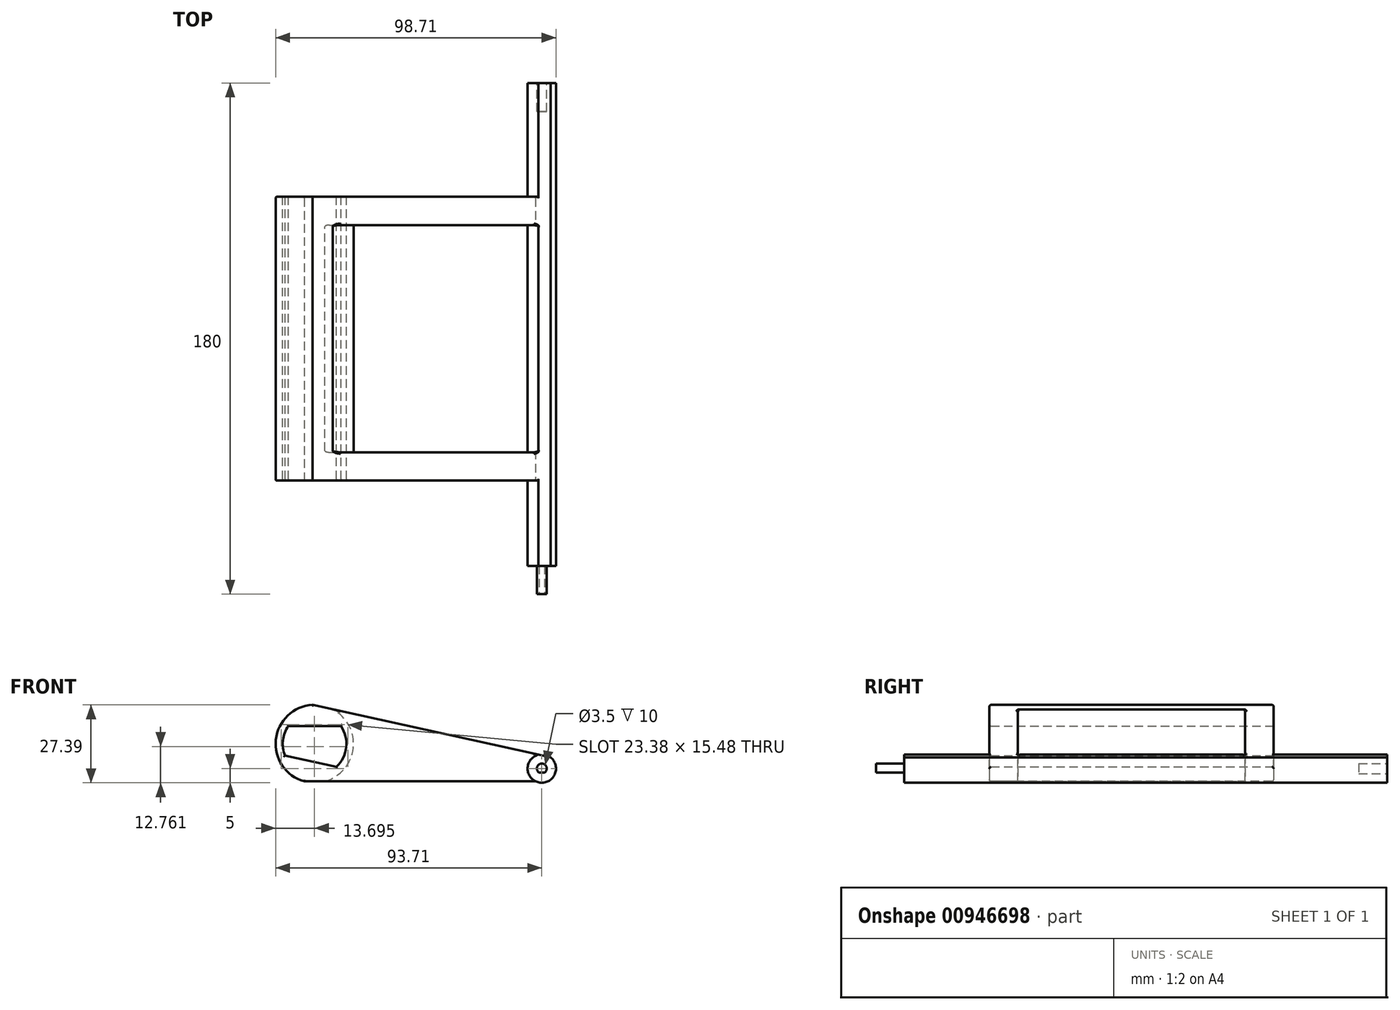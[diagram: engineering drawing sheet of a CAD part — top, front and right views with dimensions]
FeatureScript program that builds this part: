
annotation { "Feature Type Name" : "Feature", "Feature Type Description" : "" }
export const myFeature = defineFeature(function(context is Context, id is Id, definition is map)
    precondition{}
    {
        {
            var Q0;
            Q0=qCreatedBy(makeId("Front.planeOp"),FACE);
            var sketch = newSketch(context, id + "F0", { "sketchPlane" : qUnion([Q0])});
            skCircle(sketch, "E0", {"center": v(0, 0) * mm, "radius": 5 * mm});
            skCircle(sketch, "E1", {"center": v(-80, 8.7) * mm, "radius": 13.7 * mm});
            skLineSegment(sketch, "E2", {"start": v(-80, -5) * mm, "end": v(0, -5) * mm});
            skLineSegment(sketch, "E3", {"start": v(-77.05, 22.1) * mm, "end": v(1.08, 4.88) * mm});
            skCircle(sketch, "E4.0", {"center": v(-80, 8.7) * mm, "radius": 11.2 * mm});
            skLineSegment(sketch, "E5", {"start": v(-89.27, 15) * mm, "end": v(-70.73, 15) * mm});
            skLineSegment(sketch, "E6", {"start": v(-90.41, 4.56) * mm, "end": v(-72.3, 0.57) * mm});
            skSolve(sketch);
        }
        {
            var Q0;
            Q0=makeQuery(id+"F0.imprint","IMPRINT",FACE,{"disambiguationData":[TD([[makeQuery(id+"F0.imprint","IMPRINT",EDGE,{"derivedFrom":sQuery(id+"F0.wireOp",EDGE,"E0")}),1.0]])]});
            extrude(context, id + "F1", {"entities" : qUnion([Q0]), "depth" : 180 * mm, "offsetDistance" : 25 * mm, "symmetric" : true});
        }
        {
            var Q0;
            {var subQ0=sQuery(id+"F0.wireOp",EDGE,"E1");var subQ1=makeQuery(id+"F0.imprint","INTERSECT",VERTEX,{"derivedFrom":[subQ0,sQuery(id+"F0.wireOp",EDGE,"E2")]});Q0=makeQuery(id+"F0.imprint","IMPRINT",FACE,{"disambiguationData":[TD([[makeQuery(id+"F0.imprint","IMPRINT",EDGE,{"disambiguationData":[TD([[subQ1,1.0]])],"derivedFrom":subQ0}),1.0]])]});}
            var Q1;
            {var subQ0=sQuery(id+"F0.wireOp",EDGE,"E2");Q1=makeQuery(id+"F0.imprint","IMPRINT",FACE,{"disambiguationData":[TD([[makeQuery(id+"F0.imprint","IMPRINT",EDGE,{"derivedFrom":subQ0}),1.0]])]});}
            var Q2;
            {var subQ0=sQuery(id+"F0.wireOp",EDGE,"E5");Q2=makeQuery(id+"F0.imprint","IMPRINT",FACE,{"disambiguationData":[TD([[makeQuery(id+"F0.imprint","IMPRINT",EDGE,{"derivedFrom":subQ0}),1.0]])]});}
            var Q3;
            {var subQ0=sQuery(id+"F0.wireOp",EDGE,"E6");Q3=makeQuery(id+"F0.imprint","IMPRINT",FACE,{"disambiguationData":[TD([[makeQuery(id+"F0.imprint","IMPRINT",EDGE,{"derivedFrom":subQ0}),-1.0]])]});}
            extrude(context, id + "F2", {"entities" : qUnion([Q0, Q1, Q2, Q3]), "operationType" : NewBodyOperationType.ADD, "depth" : 100 * mm, "offsetDistance" : 25 * mm, "symmetric" : true});
        }
        {
            var Q0;
            {var subQ0=sQuery(id+"F0.wireOp",EDGE,"E2");Q0=makeQuery(id+"F0.imprint","IMPRINT",FACE,{"disambiguationData":[TD([[makeQuery(id+"F0.imprint","IMPRINT",EDGE,{"derivedFrom":subQ0}),1.0]])]});}
            extrude(context, id + "F3", {"entities" : qUnion([Q0]), "operationType" : NewBodyOperationType.REMOVE, "oppositeDirection" : true, "depth" : 80 * mm, "offsetDistance" : 25 * mm, "symmetric" : true});
        }
        {
            var Q0;
            Q0=makeQuery(id+"F1.opExtrude","CAP_FACE",FACE,{"disambiguationData":[OSD([sQuery(id+"F0.wireOp",EDGE,"E0")])],"isStart":false});
            var sketch = newSketch(context, id + "F4", { "sketchPlane" : qUnion([Q0])});
            skArc(sketch, "E7.0.0", {"start": v(-77.05, 22.1) * mm, "mid": v(-93.63, 10.2) * mm, "end": v(-80, -5) * mm});
            skLineSegment(sketch, "E7.0.1", {"start": v(-80, -5) * mm, "end": v(0, -5) * mm});
            skArc(sketch, "E7.0.2", {"start": v(0, -5) * mm, "mid": v(-4.97, 0.54) * mm, "end": v(1.08, 4.88) * mm});
            skLineSegment(sketch, "E7.0.3", {"start": v(1.08, 4.88) * mm, "end": v(-77.05, 22.1) * mm});
            skCircle(sketch, "E8.0", {"center": v(0, 0) * mm, "radius": 5 * mm});
            skLineSegment(sketch, "E9", {"start": v(-89.59, -4.5) * mm, "end": v(11.55, -4.5) * mm});
            skLineSegment(sketch, "E10", {"start": v(-84.5, 23.22) * mm, "end": v(10.9, 2.2) * mm});
            skSolve(sketch);
        }
        {
            var Q0;
            {var subQ0=sQuery(id+"F4.wireOp",EDGE,"E7.0.1");Q0=makeQuery(id+"F4.imprint","IMPRINT",FACE,{"disambiguationData":[TD([[makeQuery(id+"F4.imprint","IMPRINT",EDGE,{"derivedFrom":subQ0}),1.0]])]});}
            var Q1;
            {var subQ0=sQuery(id+"F4.wireOp",EDGE,"E8.0");var subQ1=makeQuery(id+"F4.imprint","INTERSECT",VERTEX,{"derivedFrom":[sQuery(id+"F4.wireOp",EDGE,"E7.0.1"),subQ0]});Q1=makeQuery(id+"F4.imprint","IMPRINT",FACE,{"disambiguationData":[TD([[makeQuery(id+"F4.imprint","IMPRINT",EDGE,{"disambiguationData":[TD([[subQ1,1.0]])],"derivedFrom":subQ0}),1.0]])]});}
            extrude(context, id + "F5", {"entities" : qUnion([Q0, Q1]), "operationType" : NewBodyOperationType.REMOVE, "endBound" : BoundingType.THROUGH_ALL, "oppositeDirection" : true, "depth" : 25 * mm, "offsetDistance" : 25 * mm});
        }
        {
            var Q0;
            {var subQ0=sQuery(id+"F4.wireOp",EDGE,"E7.0.3");Q0=makeQuery(id+"F4.imprint","IMPRINT",FACE,{"disambiguationData":[TD([[makeQuery(id+"F4.imprint","IMPRINT",EDGE,{"derivedFrom":subQ0}),1.0]])]});}
            var Q1;
            {var subQ0=sQuery(id+"F4.wireOp",EDGE,"E8.0");var subQ1=makeQuery(id+"F4.imprint","INTERSECT",VERTEX,{"derivedFrom":[sQuery(id+"F4.wireOp",EDGE,"E7.0.3"),subQ0]});Q1=makeQuery(id+"F4.imprint","IMPRINT",FACE,{"disambiguationData":[TD([[makeQuery(id+"F4.imprint","IMPRINT",EDGE,{"disambiguationData":[TD([[subQ1,1.0]])],"derivedFrom":subQ0}),1.0]])]});}
            extrude(context, id + "F6", {"entities" : qUnion([Q0, Q1]), "operationType" : NewBodyOperationType.REMOVE, "endBound" : BoundingType.THROUGH_ALL, "oppositeDirection" : true, "depth" : 25 * mm, "offsetDistance" : 25 * mm});
        }
        {
            var Q0;
            Q0=makeQuery(id+"F2.opExtrude","CAP_EDGE",EDGE,{"disambiguationData":[OSD([sQuery(id+"F0.wireOp",EDGE,"E1")])],"isStart":false});
            var Q1;
            Q1=makeQuery(id+"F2.opExtrude","CAP_EDGE",EDGE,{"disambiguationData":[OSD([sQuery(id+"F0.wireOp",EDGE,"E1")])],"isStart":true});
            var Q2;
            {var subQ0=sQuery(id+"F0.wireOp",EDGE,"E4.0");Q2=makeQuery(id+"F2.opExtrude","CAP_EDGE",EDGE,{"disambiguationData":[OSD([subQ0]),TDD([makeQuery(id+"F0.imprint","IMPRINT",EDGE,{"disambiguationData":[TD([[makeQuery(id+"F0.imprint","INTERSECT",VERTEX,{"disambiguationData":[OD(0.0)],"derivedFrom":[subQ0,sQuery(id+"F0.wireOp",EDGE,"E5")]}),-1.0]])],"derivedFrom":subQ0})])],"isStart":false});}
            var Q3;
            {var subQ0=sQuery(id+"F0.wireOp",EDGE,"E4.0");Q3=makeQuery(id+"F2.opExtrude","CAP_EDGE",EDGE,{"disambiguationData":[OSD([subQ0]),TDD([makeQuery(id+"F0.imprint","IMPRINT",EDGE,{"disambiguationData":[TD([[makeQuery(id+"F0.imprint","INTERSECT",VERTEX,{"disambiguationData":[OD(1.0)],"derivedFrom":[subQ0,sQuery(id+"F0.wireOp",EDGE,"E5")]}),1.0]])],"derivedFrom":subQ0})])],"isStart":false});}
            var Q4;
            Q4=makeQuery(id+"F2.opExtrude","CAP_EDGE",EDGE,{"disambiguationData":[OSD([sQuery(id+"F0.wireOp",EDGE,"E5")])],"isStart":false});
            var Q5;
            Q5=makeQuery(id+"F2.opExtrude","CAP_EDGE",EDGE,{"disambiguationData":[OSD([sQuery(id+"F0.wireOp",EDGE,"E6")])],"isStart":false});
            var Q6;
            Q6=makeQuery(id+"F2.opExtrude","CAP_EDGE",EDGE,{"disambiguationData":[OSD([sQuery(id+"F0.wireOp",EDGE,"E6")])],"isStart":true});
            var Q7;
            {var subQ0=sQuery(id+"F0.wireOp",EDGE,"E4.0");Q7=makeQuery(id+"F2.opExtrude","CAP_EDGE",EDGE,{"disambiguationData":[OSD([subQ0]),TDD([makeQuery(id+"F0.imprint","IMPRINT",EDGE,{"disambiguationData":[TD([[makeQuery(id+"F0.imprint","INTERSECT",VERTEX,{"disambiguationData":[OD(1.0)],"derivedFrom":[subQ0,sQuery(id+"F0.wireOp",EDGE,"E5")]}),1.0]])],"derivedFrom":subQ0})])],"isStart":true});}
            var Q8;
            {var subQ0=sQuery(id+"F0.wireOp",EDGE,"E4.0");Q8=makeQuery(id+"F2.opExtrude","CAP_EDGE",EDGE,{"disambiguationData":[OSD([subQ0]),TDD([makeQuery(id+"F0.imprint","IMPRINT",EDGE,{"disambiguationData":[TD([[makeQuery(id+"F0.imprint","INTERSECT",VERTEX,{"disambiguationData":[OD(0.0)],"derivedFrom":[subQ0,sQuery(id+"F0.wireOp",EDGE,"E5")]}),-1.0]])],"derivedFrom":subQ0})])],"isStart":true});}
            var Q9;
            Q9=makeQuery(id+"F2.opExtrude","CAP_EDGE",EDGE,{"disambiguationData":[OSD([sQuery(id+"F0.wireOp",EDGE,"E5")])],"isStart":true});
            var Q10;
            Q10=makeQuery(id+"F6.boolean.opBoolean","INTERSECT",EDGE,{"derivedFrom":[makeQuery(id+"F2.opExtrude","CAP_FACE",FACE,{"disambiguationData":[OSD([sQuery(id+"F0.wireOp",EDGE,"E0"),sQuery(id+"F0.wireOp",EDGE,"E1"),sQuery(id+"F0.wireOp",EDGE,"E2"),sQuery(id+"F0.wireOp",EDGE,"E3"),sQuery(id+"F0.wireOp",EDGE,"E4.0"),sQuery(id+"F0.wireOp",EDGE,"E5"),sQuery(id+"F0.wireOp",EDGE,"E6")])],"isStart":false}),makeQuery(id+"F6.opExtrude","SWEPT_FACE",FACE,{"disambiguationData":[OSD([sQuery(id+"F4.wireOp",EDGE,"E10")])]})]});
            var Q11;
            Q11=makeQuery(id+"F5.boolean.opBoolean","INTERSECT",EDGE,{"derivedFrom":[makeQuery(id+"F2.opExtrude","CAP_FACE",FACE,{"disambiguationData":[OSD([sQuery(id+"F0.wireOp",EDGE,"E0"),sQuery(id+"F0.wireOp",EDGE,"E1"),sQuery(id+"F0.wireOp",EDGE,"E2"),sQuery(id+"F0.wireOp",EDGE,"E3"),sQuery(id+"F0.wireOp",EDGE,"E4.0"),sQuery(id+"F0.wireOp",EDGE,"E5"),sQuery(id+"F0.wireOp",EDGE,"E6")])],"isStart":false}),makeQuery(id+"F5.opExtrude","SWEPT_FACE",FACE,{"disambiguationData":[OSD([sQuery(id+"F4.wireOp",EDGE,"E9")])]})]});
            var Q12;
            Q12=makeQuery(id+"F6.boolean.opBoolean","INTERSECT",EDGE,{"derivedFrom":[makeQuery(id+"F3.boolean.opBoolean","COPY",FACE,{"derivedFrom":makeQuery(id+"F3.opExtrude","CAP_FACE",FACE,{"disambiguationData":[OSD([sQuery(id+"F0.wireOp",EDGE,"E0"),sQuery(id+"F0.wireOp",EDGE,"E1"),sQuery(id+"F0.wireOp",EDGE,"E2"),sQuery(id+"F0.wireOp",EDGE,"E3")])],"isStart":true})}),makeQuery(id+"F6.opExtrude","SWEPT_FACE",FACE,{"disambiguationData":[OSD([sQuery(id+"F4.wireOp",EDGE,"E10")])]})]});
            var Q13;
            Q13=makeQuery(id+"F6.boolean.opBoolean","INTERSECT",EDGE,{"derivedFrom":[makeQuery(id+"F2.opExtrude","CAP_FACE",FACE,{"disambiguationData":[OSD([sQuery(id+"F0.wireOp",EDGE,"E0"),sQuery(id+"F0.wireOp",EDGE,"E1"),sQuery(id+"F0.wireOp",EDGE,"E2"),sQuery(id+"F0.wireOp",EDGE,"E3"),sQuery(id+"F0.wireOp",EDGE,"E4.0"),sQuery(id+"F0.wireOp",EDGE,"E5"),sQuery(id+"F0.wireOp",EDGE,"E6")])],"isStart":true}),makeQuery(id+"F6.opExtrude","SWEPT_FACE",FACE,{"disambiguationData":[OSD([sQuery(id+"F4.wireOp",EDGE,"E10")])]})]});
            var Q14;
            Q14=makeQuery(id+"F5.boolean.opBoolean","INTERSECT",EDGE,{"derivedFrom":[makeQuery(id+"F2.opExtrude","CAP_FACE",FACE,{"disambiguationData":[OSD([sQuery(id+"F0.wireOp",EDGE,"E0"),sQuery(id+"F0.wireOp",EDGE,"E1"),sQuery(id+"F0.wireOp",EDGE,"E2"),sQuery(id+"F0.wireOp",EDGE,"E3"),sQuery(id+"F0.wireOp",EDGE,"E4.0"),sQuery(id+"F0.wireOp",EDGE,"E5"),sQuery(id+"F0.wireOp",EDGE,"E6")])],"isStart":true}),makeQuery(id+"F5.opExtrude","SWEPT_FACE",FACE,{"disambiguationData":[OSD([sQuery(id+"F4.wireOp",EDGE,"E9")])]})]});
            var Q15;
            Q15=makeQuery(id+"F6.boolean.opBoolean","INTERSECT",EDGE,{"derivedFrom":[makeQuery(id+"F3.boolean.opBoolean","COPY",FACE,{"derivedFrom":makeQuery(id+"F3.opExtrude","CAP_FACE",FACE,{"disambiguationData":[OSD([sQuery(id+"F0.wireOp",EDGE,"E0"),sQuery(id+"F0.wireOp",EDGE,"E1"),sQuery(id+"F0.wireOp",EDGE,"E2"),sQuery(id+"F0.wireOp",EDGE,"E3")])],"isStart":false})}),makeQuery(id+"F6.opExtrude","SWEPT_FACE",FACE,{"disambiguationData":[OSD([sQuery(id+"F4.wireOp",EDGE,"E10")])]})]});
            var Q16;
            Q16=makeQuery(id+"F3.boolean.opBoolean","COPY",EDGE,{"derivedFrom":makeQuery(id+"F3.opExtrude","CAP_EDGE",EDGE,{"disambiguationData":[OSD([sQuery(id+"F0.wireOp",EDGE,"E1")])],"isStart":false})});
            var Q17;
            Q17=makeQuery(id+"F3.boolean.opBoolean","COPY",EDGE,{"derivedFrom":makeQuery(id+"F3.opExtrude","CAP_EDGE",EDGE,{"disambiguationData":[OSD([sQuery(id+"F0.wireOp",EDGE,"E1")])],"isStart":true})});
            var Q18;
            Q18=makeQuery(id+"F3.boolean.opBoolean","COPY",EDGE,{"derivedFrom":makeQuery(id+"F3.opExtrude","CAP_EDGE",EDGE,{"disambiguationData":[OSD([sQuery(id+"F0.wireOp",EDGE,"E0")])],"isStart":false})});
            var Q19;
            Q19=makeQuery(id+"F3.boolean.opBoolean","COPY",EDGE,{"derivedFrom":makeQuery(id+"F3.opExtrude","CAP_EDGE",EDGE,{"disambiguationData":[OSD([sQuery(id+"F0.wireOp",EDGE,"E0")])],"isStart":true})});
            var Q20;
            Q20=makeQuery(id+"F2.opExtrude","CAP_EDGE",EDGE,{"disambiguationData":[OSD([sQuery(id+"F0.wireOp",EDGE,"E0")])],"isStart":true});
            var Q21;
            Q21=makeQuery(id+"F2.opExtrude","CAP_EDGE",EDGE,{"disambiguationData":[OSD([sQuery(id+"F0.wireOp",EDGE,"E0")])],"isStart":false});
            fillet(context, id + "F7", {"entities" : qUnion([Q0, Q1, Q2, Q3, Q4, Q5, Q6, Q7, Q8, Q9, Q10, Q11, Q12, Q13, Q14, Q15, Q16, Q17, Q18, Q19, Q20, Q21]), "radius" : 0.5 * mm, "tangentPropagation" : true, "allowEdgeOverflow" : false});
        }
        {
            var Q0;
            Q0=makeQuery(id+"F1.opExtrude","CAP_FACE",FACE,{"disambiguationData":[OSD([sQuery(id+"F0.wireOp",EDGE,"E0")])],"isStart":false});
            var sketch = newSketch(context, id + "F8", { "sketchPlane" : qUnion([Q0])});
            skCircle(sketch, "E11", {"center": v(0, 0) * mm, "radius": 1.75 * mm});
            skLineSegment(sketch, "E12", {"start": v(-0.98, -1.45) * mm, "end": v(0.98, -1.45) * mm});
            skSolve(sketch);
        }
        {
            var Q0;
            Q0=makeQuery(id+"F8.imprint","IMPRINT",FACE,{"disambiguationData":[TD([[makeQuery(id+"F8.imprint","IMPRINT",EDGE,{"derivedFrom":sQuery(id+"F8.wireOp",EDGE,"E11")}),-1.0]])]});
            var Q1;
            {var subQ0=sQuery(id+"F8.wireOp",EDGE,"E12");Q1=makeQuery(id+"F8.imprint","IMPRINT",FACE,{"disambiguationData":[TD([[makeQuery(id+"F8.imprint","IMPRINT",EDGE,{"derivedFrom":subQ0}),-1.0]])]});}
            extrude(context, id + "F9", {"entities" : qUnion([Q0, Q1]), "operationType" : NewBodyOperationType.REMOVE, "oppositeDirection" : true, "depth" : 10 * mm, "offsetDistance" : 25 * mm});
        }
        {
            var Q0;
            Q0=makeQuery(id+"F1.opExtrude","CAP_FACE",FACE,{"disambiguationData":[OSD([sQuery(id+"F0.wireOp",EDGE,"E0")])],"isStart":true});
            var sketch = newSketch(context, id + "F10", { "sketchPlane" : qUnion([Q0])});
            skCircle(sketch, "E13.0", {"center": v(0, 0) * mm, "radius": 1.75 * mm});
            skLineSegment(sketch, "E14.0", {"start": v(0.98, -1.45) * mm, "end": v(-0.98, -1.45) * mm});
            skSolve(sketch);
        }
        {
            var Q0;
            Q0=makeQuery(id+"F10.imprint","IMPRINT",FACE,{"disambiguationData":[TD([[makeQuery(id+"F10.imprint","IMPRINT",EDGE,{"derivedFrom":sQuery(id+"F10.wireOp",EDGE,"E13.0")}),1.0]])]});
            var Q1;
            {var subQ0=sQuery(id+"F10.wireOp",EDGE,"E14.0");Q1=makeQuery(id+"F10.imprint","IMPRINT",FACE,{"disambiguationData":[TD([[makeQuery(id+"F10.imprint","IMPRINT",EDGE,{"derivedFrom":subQ0}),1.0]])]});}
            extrude(context, id + "F11", {"entities" : qUnion([Q0, Q1]), "operationType" : NewBodyOperationType.REMOVE, "oppositeDirection" : true, "depth" : 10 * mm, "offsetDistance" : 25 * mm});
        }
    });
